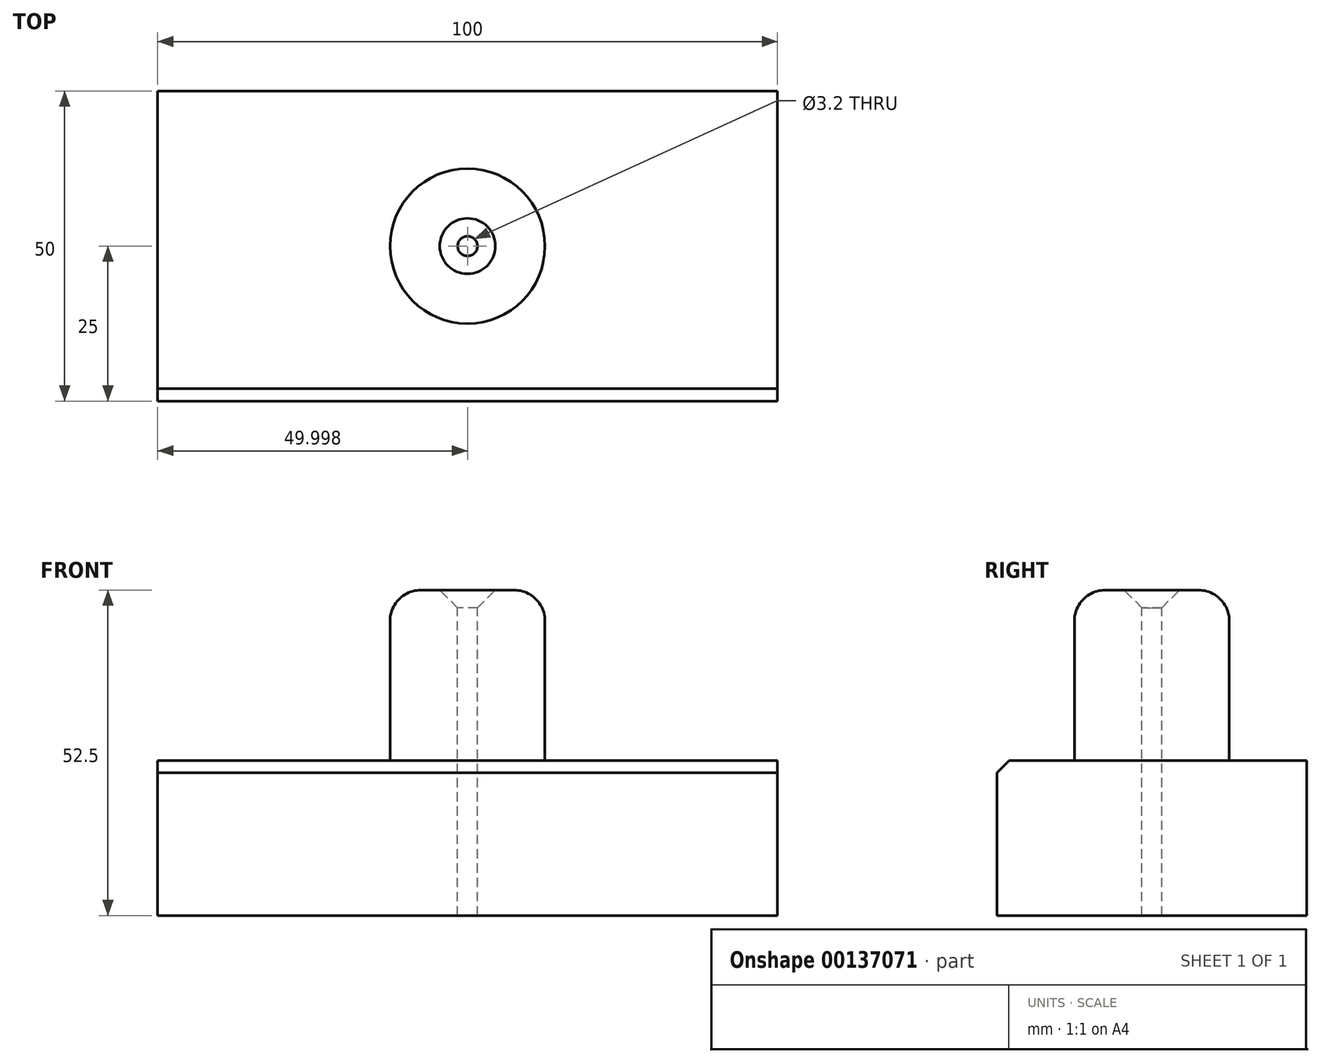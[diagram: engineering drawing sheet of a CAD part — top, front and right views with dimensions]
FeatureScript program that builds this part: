
annotation { "Feature Type Name" : "Feature", "Feature Type Description" : "" }
export const myFeature = defineFeature(function(context is Context, id is Id, definition is map)
    precondition{}
    {
        {
            var Q0;
            Q0=qCreatedBy(makeId("Front.planeOp"),FACE);
            var sketch = newSketch(context, id + "F0", { "sketchPlane" : qUnion([Q0])});
            skLineSegment(sketch, "E0.bottom", {"start": v(50.3, -14.19) * mm, "end": v(-49.7, -14.19) * mm});
            skLineSegment(sketch, "E0.top", {"start": v(50.3, 10.81) * mm, "end": v(-49.7, 10.81) * mm});
            skLineSegment(sketch, "E0.left", {"start": v(50.3, -14.19) * mm, "end": v(50.3, 10.81) * mm});
            skLineSegment(sketch, "E0.right", {"start": v(-49.7, -14.19) * mm, "end": v(-49.7, 10.81) * mm});
            skPoint(sketch, "E0.middle", {"position": v(0.3, -1.69) * mm});
            skSolve(sketch);
        }
        {
            var Q0;
            Q0=makeQuery(id+"F0.imprint","IMPRINT",FACE,{"disambiguationData":[TD([[makeQuery(id+"F0.imprint","IMPRINT",EDGE,{"derivedFrom":sQuery(id+"F0.wireOp",EDGE,"E0.bottom")}),-1.0]])]});
            extrude(context, id + "F1", {"entities" : qUnion([Q0]), "depth" : 50 * mm});
        }
        {
            var Q0;
            Q0=makeQuery(id+"F1.opExtrude","CAP_EDGE",EDGE,{"disambiguationData":[OSD([sQuery(id+"F0.wireOp",EDGE,"E0.top")])],"isStart":false});
            chamfer(context, id + "F2", {"entities" : qUnion([Q0]), "width" : 2 * mm, "tangentPropagation" : true});
        }
        {
            var Q0;
            Q0=makeQuery(id+"F1.opExtrude","SWEPT_FACE",FACE,{"disambiguationData":[OSD([sQuery(id+"F0.wireOp",EDGE,"E0.top")])]});
            var sketch = newSketch(context, id + "F3", { "sketchPlane" : qUnion([Q0])});
            skCircle(sketch, "E1", {"center": v(0.3, -25) * mm, "radius": 12.5 * mm});
            skSolve(sketch);
        }
        {
            var Q0;
            Q0=makeQuery(id+"F3.imprint","IMPRINT",FACE,{"disambiguationData":[TD([[makeQuery(id+"F3.imprint","IMPRINT",EDGE,{"derivedFrom":sQuery(id+"F3.wireOp",EDGE,"E1")}),1.0]])]});
            extrude(context, id + "F4", {"entities" : qUnion([Q0]), "operationType" : NewBodyOperationType.ADD, "depth" : 27.5 * mm});
        }
        {
            var Q0;
            Q0=makeQuery(id+"F4.opExtrude","CAP_EDGE",EDGE,{"disambiguationData":[OSD([sQuery(id+"F3.wireOp",EDGE,"E1")])],"isStart":false});
            fillet(context, id + "F5", {"entities" : qUnion([Q0]), "radius" : 5 * mm, "tangentPropagation" : true, "allowEdgeOverflow" : false});
        }
        {
            var Q0;
            Q0=makeQuery(id+"F4.opExtrude","CAP_FACE",FACE,{"disambiguationData":[OSD([sQuery(id+"F3.wireOp",EDGE,"E1")])],"isStart":false});
            var sketch = newSketch(context, id + "F6", { "sketchPlane" : qUnion([Q0])});
            skPoint(sketch, "E2", {"position": v(0.3, -25) * mm});
            skSolve(sketch);
        }
        {
            var Q0;
            Q0=sQuery(id+"F6.wireOp",VERTEX,"E2");
            var Q1;
            Q1=makeQuery(id+"F1.opExtrude","SWEPT_BODY",BODY,{"disambiguationData":[OSD([sQuery(id+"F0.wireOp",EDGE,"E0.bottom"),sQuery(id+"F0.wireOp",EDGE,"E0.top"),sQuery(id+"F0.wireOp",EDGE,"E0.left"),sQuery(id+"F0.wireOp",EDGE,"E0.right")])]});
            hole(context, id + "F7", {"style" : HoleStyle.C_SINK, "endStyle" : HoleEndStyle.THROUGH, "standardTappedOrClearance" : lookupTablePath({ "standard" : "ISO", "engagement" : "75%", "pitch" : "0.75 mm", "size" : "M4", "type" : "Tapped" }), "standardBlindInLast" : lookupTablePath({ "standard" : "ISO", "engagement" : "75%", "pitch" : "0.75 mm", "size" : "M4", "type" : "Tapped" }), "holeDiameter" : 3.2 * mm, "cSinkDiameter" : 8.96 * mm, "cSinkAngle" : 90 * degree, "startFromSketch" : true, "locations" : qUnion([Q0]), "scope" : qUnion([Q1]), "isTappedThrough" : true, "showTappedDepth" : true});
        }
    });
